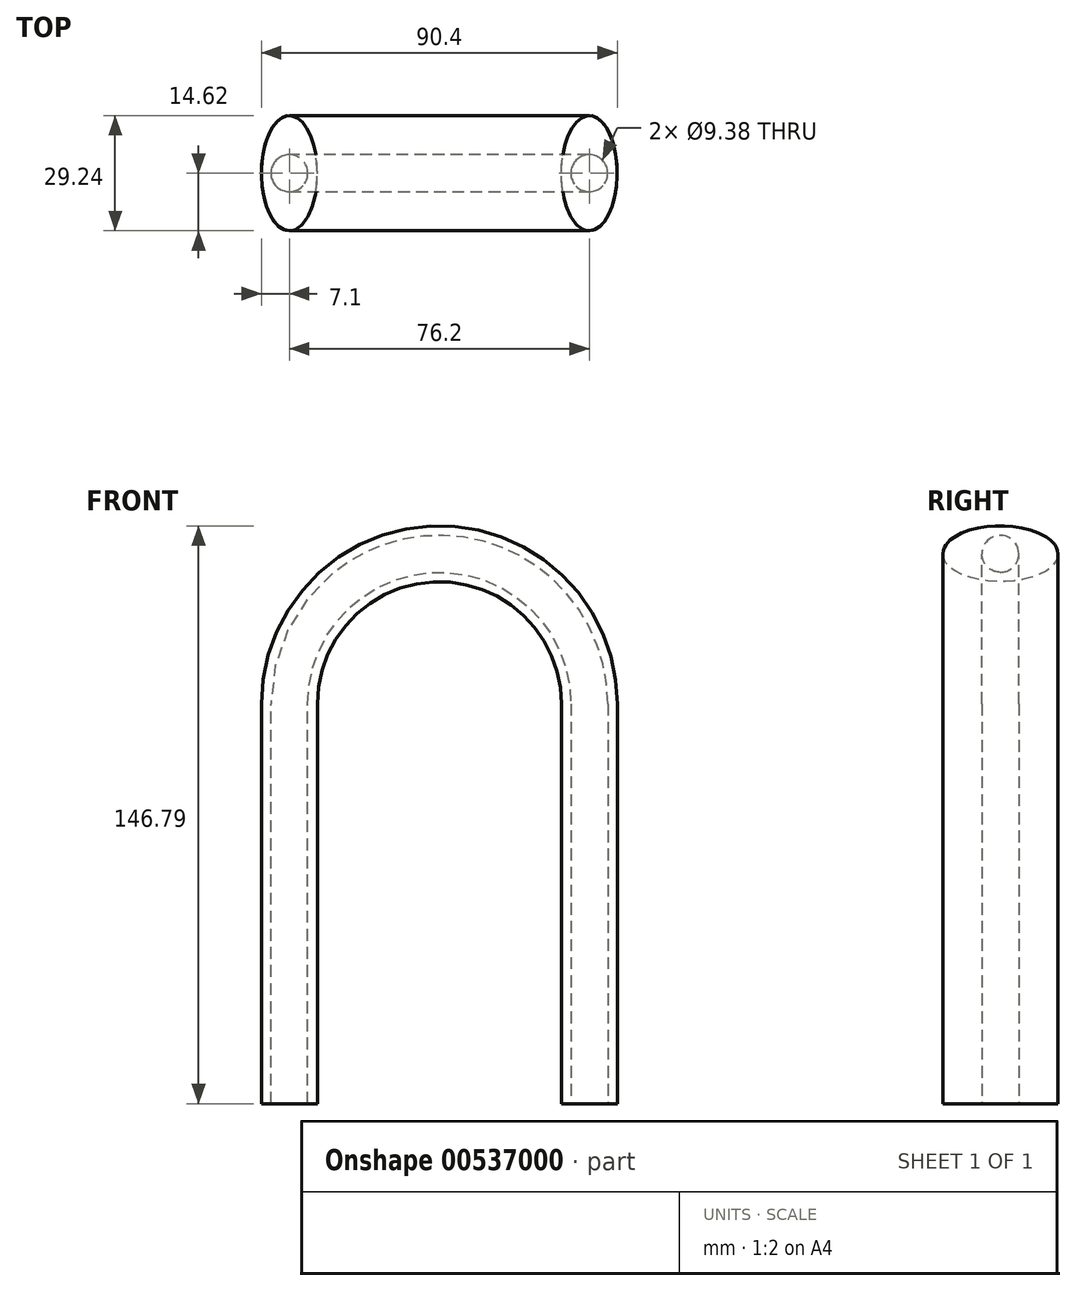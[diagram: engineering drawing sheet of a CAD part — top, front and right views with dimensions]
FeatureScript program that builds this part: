
annotation { "Feature Type Name" : "Feature", "Feature Type Description" : "" }
export const myFeature = defineFeature(function(context is Context, id is Id, definition is map)
    precondition{}
    {
        {
            var Q0;
            Q0=qCreatedBy(makeId("Front.planeOp"),FACE);
            var sketch = newSketch(context, id + "F0", { "sketchPlane" : qUnion([Q0])});
            skLineSegment(sketch, "E0", {"start": v(0, 0) * mm, "end": v(0, 101.6) * mm});
            skLineSegment(sketch, "E1", {"start": v(76.2, 101.6) * mm, "end": v(76.2, 0) * mm});
            skArc(sketch, "E2", {"start": v(76.2, 101.6) * mm, "mid": v(38.1, 139.7) * mm, "end": v(0, 101.6) * mm});
            skSolve(sketch);
        }
        {
            var Q0;
            Q0=qCreatedBy(makeId("Top.planeOp"),FACE);
            var sketch = newSketch(context, id + "F1", { "sketchPlane" : qUnion([Q0])});
            skEllipse(sketch, "E3", {"center": v(0, 0) * mm, "majorRadius": 14.62 * mm, "minorRadius": 7.1 * mm, "majorAxis": v(0, -1)});
            skCircle(sketch, "E4", {"center": v(0, 0) * mm, "radius": 4.69 * mm});
            skSolve(sketch);
        }
        {
            var Q0;
            Q0=makeQuery(id+"F1.imprint","IMPRINT",FACE,{"disambiguationData":[TD([[makeQuery(id+"F1.imprint","IMPRINT",EDGE,{"derivedFrom":sQuery(id+"F1.wireOp",EDGE,"E3")}),1.0]])]});
            var Q1;
            Q1=sQuery(id+"F0.wireOp",EDGE,"E0");
            var Q2;
            Q2=sQuery(id+"F0.wireOp",EDGE,"E2");
            var Q3;
            Q3=sQuery(id+"F0.wireOp",EDGE,"E1");
            sweep(context, id + "F2", {"profiles" : qUnion([Q0]), "path" : qUnion([Q1, Q2, Q3])});
        }
    });
